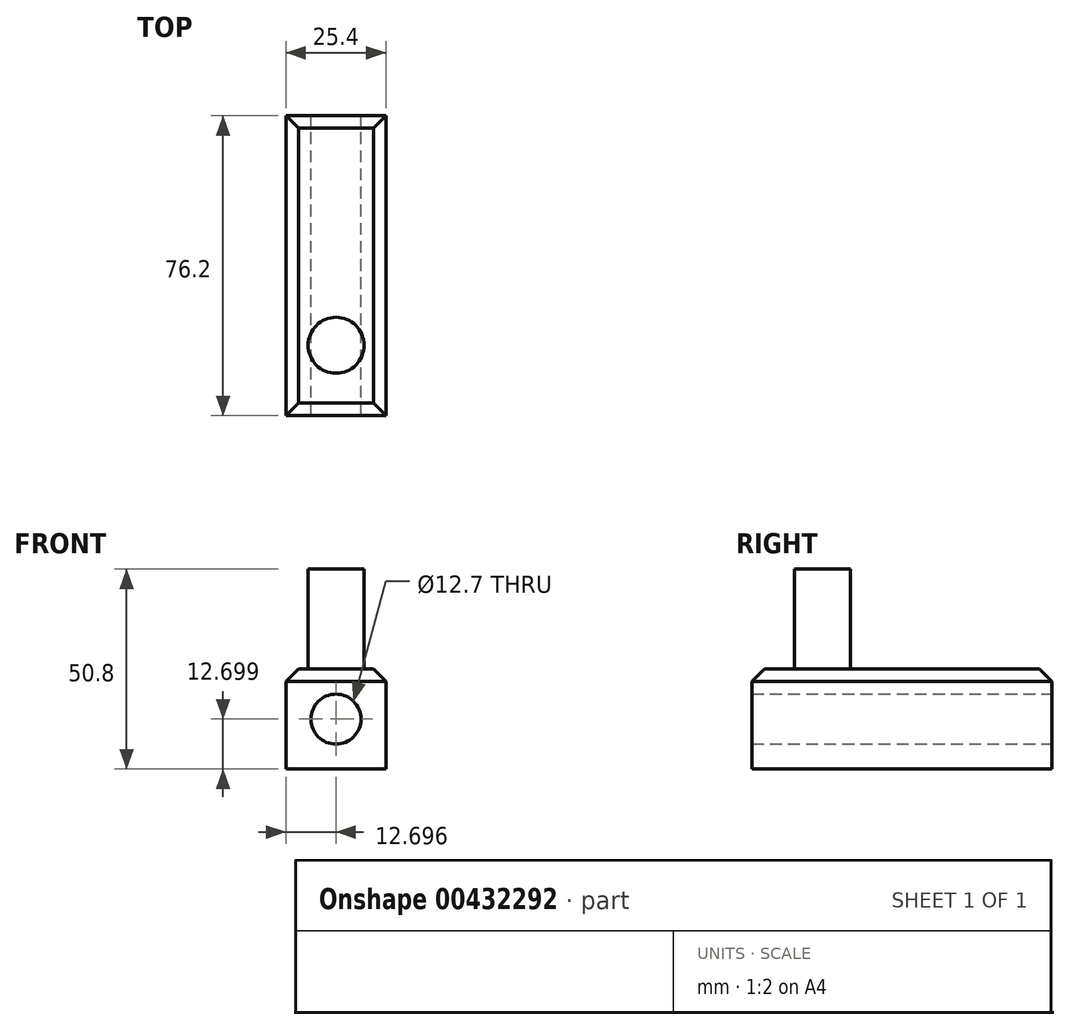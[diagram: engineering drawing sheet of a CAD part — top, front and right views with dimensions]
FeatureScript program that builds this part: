
annotation { "Feature Type Name" : "Feature", "Feature Type Description" : "" }
export const myFeature = defineFeature(function(context is Context, id is Id, definition is map)
    precondition{}
    {
        {
            var Q0;
            Q0=qCreatedBy(makeId("Front.planeOp"),FACE);
            var sketch = newSketch(context, id + "F0", { "sketchPlane" : qUnion([Q0])});
            skLineSegment(sketch, "E0.bottom", {"start": v(-44.76, 50.08) * mm, "end": v(-19.36, 50.08) * mm});
            skLineSegment(sketch, "E0.top", {"start": v(-44.76, 24.68) * mm, "end": v(-19.36, 24.68) * mm});
            skLineSegment(sketch, "E0.left", {"start": v(-44.76, 50.08) * mm, "end": v(-44.76, 24.68) * mm});
            skLineSegment(sketch, "E0.right", {"start": v(-19.36, 50.08) * mm, "end": v(-19.36, 24.68) * mm});
            skCircle(sketch, "E1", {"center": v(-32.06, 37.38) * mm, "radius": 6.35 * mm});
            skSolve(sketch);
        }
        {
            var Q0;
            Q0=makeQuery(id+"F0.imprint","IMPRINT",FACE,{"disambiguationData":[TD([[makeQuery(id+"F0.imprint","IMPRINT",EDGE,{"derivedFrom":sQuery(id+"F0.wireOp",EDGE,"E0.bottom")}),-1.0]])]});
            extrude(context, id + "F1", {"entities" : qUnion([Q0]), "depth" : 76.2 * mm});
        }
        {
            var Q0;
            Q0=makeQuery(id+"F1.opExtrude","SWEPT_FACE",FACE,{"disambiguationData":[OSD([sQuery(id+"F0.wireOp",EDGE,"E0.bottom")])]});
            var sketch = newSketch(context, id + "F2", { "sketchPlane" : qUnion([Q0])});
            skCircle(sketch, "E2", {"center": v(-32.02, -58.3) * mm, "radius": 7.1 * mm});
            skSolve(sketch);
        }
        {
            var Q0;
            Q0=makeQuery(id+"F2.imprint","IMPRINT",FACE,{"disambiguationData":[TD([[makeQuery(id+"F2.imprint","IMPRINT",EDGE,{"derivedFrom":sQuery(id+"F2.wireOp",EDGE,"E2")}),1.0]])]});
            extrude(context, id + "F3", {"entities" : qUnion([Q0]), "operationType" : NewBodyOperationType.ADD, "depth" : 25.4 * mm});
        }
        {
            var Q0;
            Q0=makeQuery(id+"F1.opExtrude","SWEPT_EDGE",EDGE,{"disambiguationData":[OSD([sQuery(id+"F0.wireOp",EDGE,"E0.bottom"),sQuery(id+"F0.wireOp",EDGE,"E0.right")])]});
            var Q1;
            Q1=makeQuery(id+"F1.opExtrude","CAP_EDGE",EDGE,{"disambiguationData":[OSD([sQuery(id+"F0.wireOp",EDGE,"E0.bottom")])],"isStart":false});
            var Q2;
            Q2=makeQuery(id+"F1.opExtrude","SWEPT_EDGE",EDGE,{"disambiguationData":[OSD([sQuery(id+"F0.wireOp",EDGE,"E0.bottom"),sQuery(id+"F0.wireOp",EDGE,"E0.left")])]});
            var Q3;
            Q3=makeQuery(id+"F1.opExtrude","CAP_EDGE",EDGE,{"disambiguationData":[OSD([sQuery(id+"F0.wireOp",EDGE,"E0.bottom")])],"isStart":true});
            chamfer(context, id + "F4", {"entities" : qUnion([Q0, Q1, Q2, Q3]), "width" : 3.17 * mm, "tangentPropagation" : true});
        }
    });
